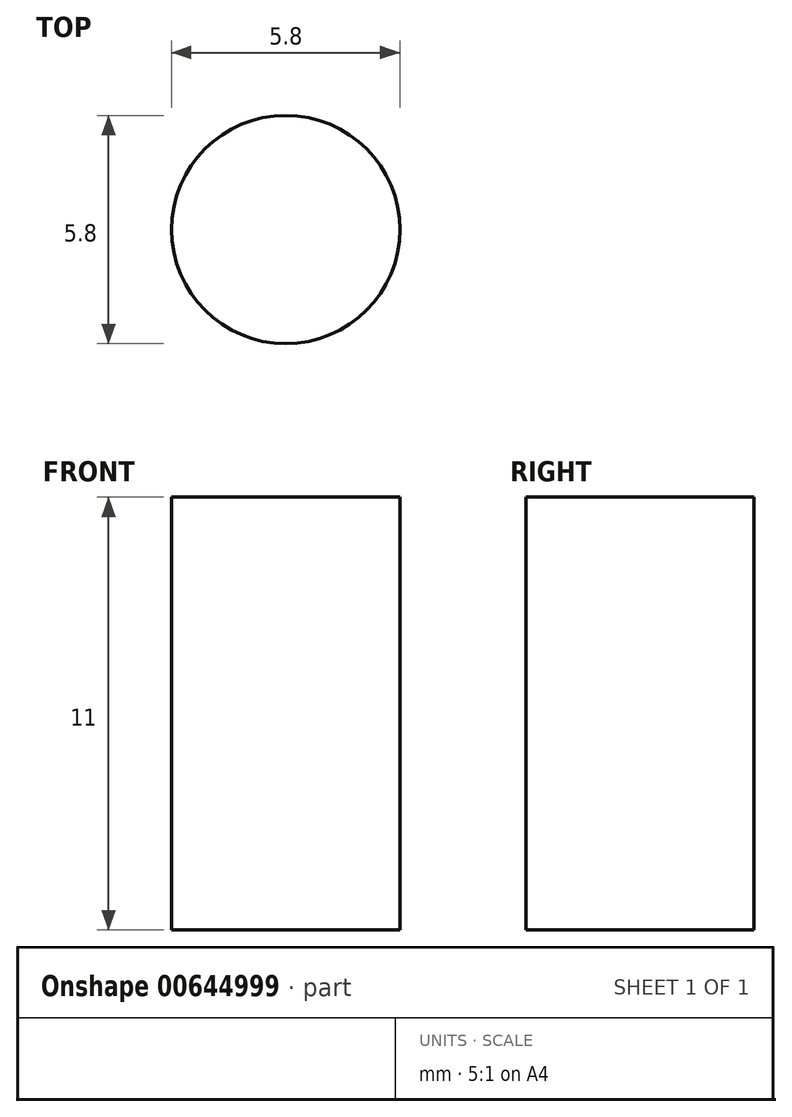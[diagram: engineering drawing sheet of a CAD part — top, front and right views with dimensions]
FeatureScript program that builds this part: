
annotation { "Feature Type Name" : "Feature", "Feature Type Description" : "" }
export const myFeature = defineFeature(function(context is Context, id is Id, definition is map)
    precondition{}
    {
        {
            var Q0;
            Q0=qCreatedBy(makeId("Top.planeOp"),FACE);
            var sketch = newSketch(context, id + "F0", { "sketchPlane" : qUnion([Q0])});
            skCircle(sketch, "E0", {"center": v(0, 0) * mm, "radius": 2.9 * mm});
            skSolve(sketch);
        }
        {
            var Q0;
            Q0 = qSketchRegion(id + "F0", true);
            extrude(context, id + "F1", {"entities" : qUnion([Q0]), "endBound" : BoundingType.SYMMETRIC, "depth" : 11 * mm, "offsetDistance" : 25 * mm});
        }
    });
